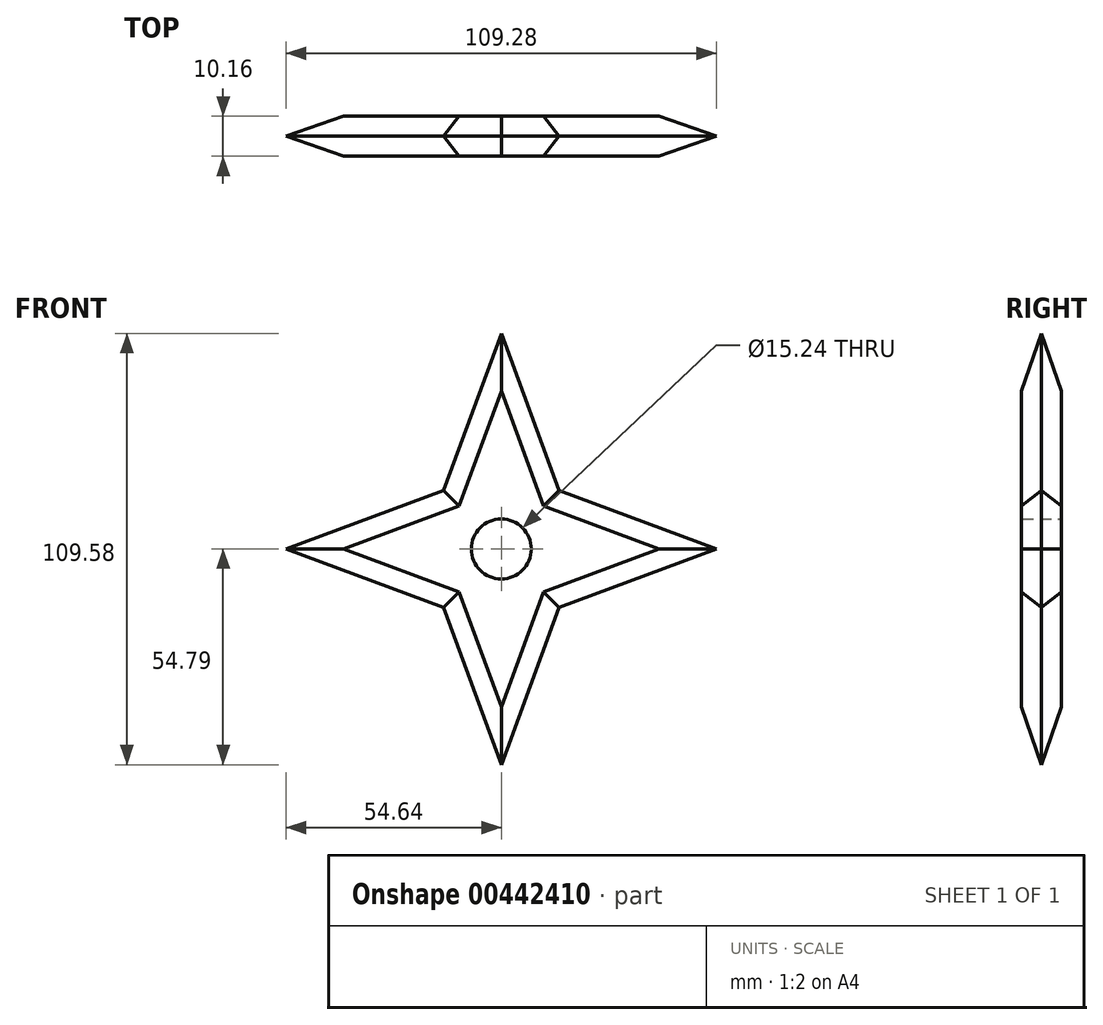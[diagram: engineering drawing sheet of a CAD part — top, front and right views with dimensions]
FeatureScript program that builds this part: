
annotation { "Feature Type Name" : "Feature", "Feature Type Description" : "" }
export const myFeature = defineFeature(function(context is Context, id is Id, definition is map)
    precondition{}
    {
        {
            var Q0;
            Q0=qCreatedBy(makeId("Front.planeOp"),FACE);
            var sketch = newSketch(context, id + "F0", { "sketchPlane" : qUnion([Q0])});
            skLineSegment(sketch, "E0", {"start": v(0, 54.8) * mm, "end": v(14.71, 14.86) * mm});
            skLineSegment(sketch, "E1", {"start": v(14.71, 14.86) * mm, "end": v(0, 0) * mm});
            skLineSegment(sketch, "E2.MirrorCS", {"start": v(0, 54.8) * mm, "end": v(-14.71, 14.86) * mm});
            skLineSegment(sketch, "E3.MirrorCS", {"start": v(-14.71, 14.86) * mm, "end": v(0, 0) * mm});
            skLineSegment(sketch, "E4", {"start": v(0, 0) * mm, "end": v(14.71, -14.86) * mm});
            skLineSegment(sketch, "E5", {"start": v(14.71, -14.86) * mm, "end": v(0, -54.8) * mm});
            skLineSegment(sketch, "E6.MirrorCS", {"start": v(-14.71, -14.86) * mm, "end": v(0, -54.8) * mm});
            skLineSegment(sketch, "E7.MirrorCS", {"start": v(0, 0) * mm, "end": v(-14.71, -14.86) * mm});
            skLineSegment(sketch, "E8", {"start": v(-14.71, 14.86) * mm, "end": v(-54.64, 0) * mm});
            skLineSegment(sketch, "E9", {"start": v(-54.64, 0) * mm, "end": v(-14.71, -14.86) * mm});
            skLineSegment(sketch, "E10", {"start": v(14.71, 14.86) * mm, "end": v(54.64, 0) * mm});
            skLineSegment(sketch, "E11", {"start": v(54.64, 0) * mm, "end": v(14.71, -14.86) * mm});
            skSolve(sketch);
        }
        {
            var Q0;
            Q0=makeQuery(id+"F0.imprint","IMPRINT",FACE,{"disambiguationData":[TD([[makeQuery(id+"F0.imprint","IMPRINT",EDGE,{"derivedFrom":sQuery(id+"F0.wireOp",EDGE,"E0")}),-1.0]])]});
            var Q1;
            Q1=makeQuery(id+"F0.imprint","IMPRINT",FACE,{"disambiguationData":[TD([[makeQuery(id+"F0.imprint","IMPRINT",EDGE,{"derivedFrom":sQuery(id+"F0.wireOp",EDGE,"E1")}),1.0]])]});
            var Q2;
            Q2=makeQuery(id+"F0.imprint","IMPRINT",FACE,{"disambiguationData":[TD([[makeQuery(id+"F0.imprint","IMPRINT",EDGE,{"derivedFrom":sQuery(id+"F0.wireOp",EDGE,"E4")}),-1.0]])]});
            var Q3;
            Q3=makeQuery(id+"F0.imprint","IMPRINT",FACE,{"disambiguationData":[TD([[makeQuery(id+"F0.imprint","IMPRINT",EDGE,{"derivedFrom":sQuery(id+"F0.wireOp",EDGE,"E3.MirrorCS")}),-1.0]])]});
            extrude(context, id + "F1", {"entities" : qUnion([Q0, Q1, Q2, Q3]), "depth" : 10.16 * mm});
        }
        {
            var Q0;
            Q0=makeQuery(id+"F1.opExtrude","CAP_EDGE",EDGE,{"disambiguationData":[OSD([sQuery(id+"F0.wireOp",EDGE,"E0")])],"isStart":true});
            var Q1;
            Q1=makeQuery(id+"F1.opExtrude","CAP_EDGE",EDGE,{"disambiguationData":[OSD([sQuery(id+"F0.wireOp",EDGE,"E2.MirrorCS")])],"isStart":true});
            var Q2;
            Q2=makeQuery(id+"F1.opExtrude","CAP_EDGE",EDGE,{"disambiguationData":[OSD([sQuery(id+"F0.wireOp",EDGE,"E2.MirrorCS")])],"isStart":false});
            var Q3;
            Q3=makeQuery(id+"F1.opExtrude","CAP_EDGE",EDGE,{"disambiguationData":[OSD([sQuery(id+"F0.wireOp",EDGE,"E0")])],"isStart":false});
            var Q4;
            Q4=makeQuery(id+"F1.opExtrude","CAP_EDGE",EDGE,{"disambiguationData":[OSD([sQuery(id+"F0.wireOp",EDGE,"E8")])],"isStart":false});
            var Q5;
            Q5=makeQuery(id+"F1.opExtrude","CAP_EDGE",EDGE,{"disambiguationData":[OSD([sQuery(id+"F0.wireOp",EDGE,"E8")])],"isStart":true});
            var Q6;
            Q6=makeQuery(id+"F1.opExtrude","CAP_EDGE",EDGE,{"disambiguationData":[OSD([sQuery(id+"F0.wireOp",EDGE,"E9")])],"isStart":false});
            var Q7;
            Q7=makeQuery(id+"F1.opExtrude","CAP_EDGE",EDGE,{"disambiguationData":[OSD([sQuery(id+"F0.wireOp",EDGE,"E9")])],"isStart":true});
            var Q8;
            Q8=makeQuery(id+"F1.opExtrude","CAP_EDGE",EDGE,{"disambiguationData":[OSD([sQuery(id+"F0.wireOp",EDGE,"E11")])],"isStart":true});
            var Q9;
            Q9=makeQuery(id+"F1.opExtrude","CAP_EDGE",EDGE,{"disambiguationData":[OSD([sQuery(id+"F0.wireOp",EDGE,"E10")])],"isStart":true});
            var Q10;
            Q10=makeQuery(id+"F1.opExtrude","CAP_EDGE",EDGE,{"disambiguationData":[OSD([sQuery(id+"F0.wireOp",EDGE,"E10")])],"isStart":false});
            var Q11;
            Q11=makeQuery(id+"F1.opExtrude","CAP_EDGE",EDGE,{"disambiguationData":[OSD([sQuery(id+"F0.wireOp",EDGE,"E11")])],"isStart":false});
            var Q12;
            Q12=makeQuery(id+"F1.opExtrude","CAP_EDGE",EDGE,{"disambiguationData":[OSD([sQuery(id+"F0.wireOp",EDGE,"E6.MirrorCS")])],"isStart":true});
            var Q13;
            Q13=makeQuery(id+"F1.opExtrude","CAP_EDGE",EDGE,{"disambiguationData":[OSD([sQuery(id+"F0.wireOp",EDGE,"E5")])],"isStart":true});
            var Q14;
            Q14=makeQuery(id+"F1.opExtrude","CAP_EDGE",EDGE,{"disambiguationData":[OSD([sQuery(id+"F0.wireOp",EDGE,"E6.MirrorCS")])],"isStart":false});
            var Q15;
            Q15=makeQuery(id+"F1.opExtrude","CAP_EDGE",EDGE,{"disambiguationData":[OSD([sQuery(id+"F0.wireOp",EDGE,"E5")])],"isStart":false});
            chamfer(context, id + "F2", {"entities" : qUnion([Q0, Q1, Q2, Q3, Q4, Q5, Q6, Q7, Q8, Q9, Q10, Q11, Q12, Q13, Q14, Q15]), "width" : 5.08 * mm, "tangentPropagation" : true});
        }
        {
            var Q0;
            Q0=qCreatedBy(makeId("Front.planeOp"),FACE);
            var sketch = newSketch(context, id + "F3", { "sketchPlane" : qUnion([Q0])});
            skPoint(sketch, "E12", {"position": v(0, 0) * mm});
            skSolve(sketch);
        }
        {
            var Q0;
            Q0=sQuery(id+"F3.wireOp",VERTEX,"E12");
            var Q1;
            Q1=makeQuery(id+"F1.opExtrude","SWEPT_BODY",BODY,{"disambiguationData":[OSD([sQuery(id+"F0.wireOp",EDGE,"E0"),sQuery(id+"F0.wireOp",EDGE,"E2.MirrorCS"),sQuery(id+"F0.wireOp",EDGE,"E5"),sQuery(id+"F0.wireOp",EDGE,"E6.MirrorCS"),sQuery(id+"F0.wireOp",EDGE,"E8"),sQuery(id+"F0.wireOp",EDGE,"E9"),sQuery(id+"F0.wireOp",EDGE,"E10"),sQuery(id+"F0.wireOp",EDGE,"E11")])]});
            hole(context, id + "F4", {"style" : HoleStyle.SIMPLE, "endStyle" : HoleEndStyle.THROUGH, "oppositeDirection" : true, "holeDiameter" : 15.24 * mm, "isTappedThrough" : true, "tappedDepth" : 12.7 * mm, "tapClearance" : 3, "locations" : qUnion([Q0]), "scope" : qUnion([Q1])});
        }
    });
